# Revit family: Trägeranbindung IB vertikal, Typ D III und IV
name_source: partatom
category: HLS-Bauteile
revit_build: Autodesk Revit 2017 (Build: 20190507_1515(x64)
units: mm (PartAtom-declared; Revit-internal decimal feet)

## family parameters
Arbeitsebenenbasiert = Nein
Beim Laden mit Abzugskörper schneiden = Nein
Bemaßung runder Anschluss = Durchmesser verwenden
Gemeinsam genutzt = Ja
Immer vertikal = Nein
Raumberechnungspunkt = Nein
Teiletyp = Normal

## types (2) — shared parameters
Fabrikat = MEFA
Firma = MEFA Befestigungs- und Montagesysteme GmbH
Kurztext1 = Trägeranbindung IB C-Profil 45
Material = Stahl
Materialname = S235
Mengeneinheit = St
Oberflaeche = feuerstückverzinkt
max. zul. Last Zug = 4.00 kN
max. zul. Schublast = 4.00 kN
vpe = 1 St
zero-valued in all types: max Klemmdicke, max. Klemmstärke

## per-type parameters (varying)
| type | AB | Artikelnummer | EAN | Gewicht | Gewicht pro Bauteil | Gewindestange | Gewindestangentyp | Klemmweite | Klemmweite Flansch | Klemmweite Flansch max. | Klemmweite Flansch min. | Kurztext2 | Trägeranbindung IB | Typ | min. Klemmdicke |
| Trägeranbindung IB vertikal, Typ D III | 120 mm  [stored 0.393701 ft] | 08146103 | 4250928420084 | 1.13 kg | 1.13 kg | Gewindestift FK 8.8 mm : Gewindestange M12x310 mm | M12 x 310 | 100-220 mm | 220 mm  [stored 0.721785 ft] | 220 mm  [stored 0.721785 ft] | 100 mm  [stored 0.328084 ft] | Typ D III Klemmdicke 8 - 15 mm | Trägeranbindung rechts IB12 | D III | 8 mm |
| Trägeranbindung IB vertikal, Typ D IV | 250 mm | 08146104 | 4250928420091 | 2.05 kg | 2.05 kg | Gewindestift FK 8.8 mm : Gewindestange M16x500 mm | M16 x 500 | 110-360 mm | 360 mm  [stored 1.1811 ft] | 360 mm  [stored 1.1811 ft] | 110 mm  [stored 0.360892 ft] | Typ D IV Klemmdicke 13 - 20 mm | Trägeranbindung rechts IB16 | D IV | 13 mm |

note: [stored X ft] marks values corroborated as IEEE doubles in the binary element streams (Revit-internal decimal feet)

## geometry (parser evidence)
native form markers: Sweep x6
no freeform markers — native parametric forms only
